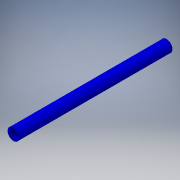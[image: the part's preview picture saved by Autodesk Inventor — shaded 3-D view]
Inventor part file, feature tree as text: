
AUTODESK INVENTOR PART (.ipt)
format: ipt  version: 2018.2 (Build 222227000, 227)  size: 105,472 bytes
history: native  units: in
note: dims shown in document units (in); Inventor stores cm internally (conversion verified against a paired STEP export)
features: extrude x1, sketch x1
ambient origin geometry x8: Origin, YZ Plane, XZ Plane, XY Plane, X Axis, Y Axis, Z Axis, Center Point
bodies: Solid1 (feature_tree)
feature tree (2):
  extrude  "Extrusion1"  Depth=17.25in
  sketch  "Sketch1"  dims[d0=1.315in d1=1.0in d2=17.25in d3=0.0in]
